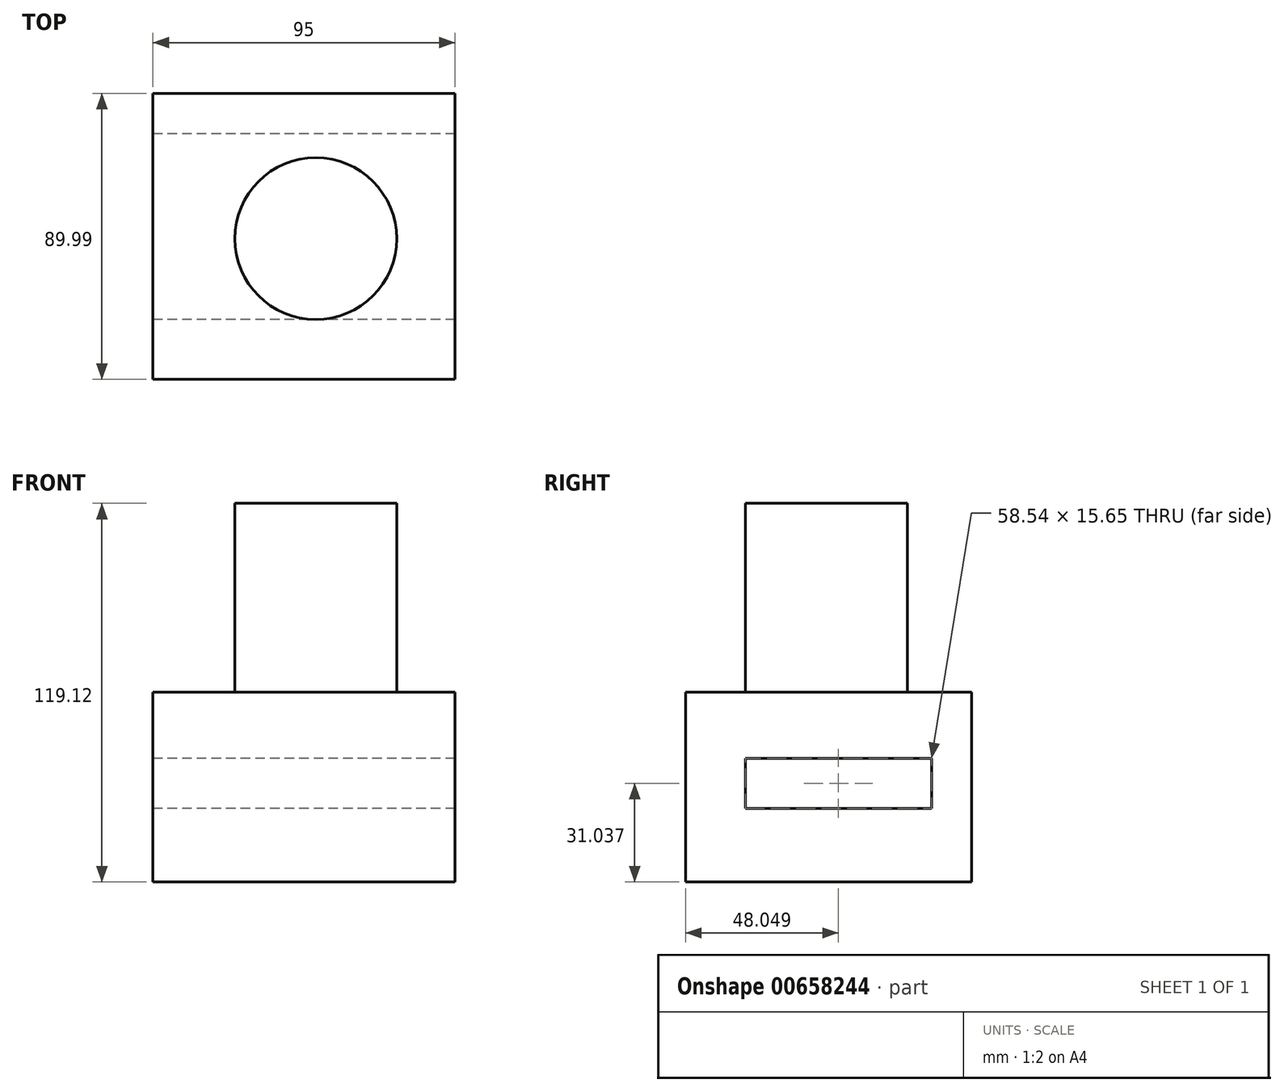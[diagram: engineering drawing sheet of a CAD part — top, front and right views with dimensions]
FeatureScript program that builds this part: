
annotation { "Feature Type Name" : "Feature", "Feature Type Description" : "" }
export const myFeature = defineFeature(function(context is Context, id is Id, definition is map)
    precondition{}
    {
        {
            var Q0;
            Q0=qCreatedBy(makeId("Right.planeOp"),FACE);
            var sketch = newSketch(context, id + "F0", { "sketchPlane" : qUnion([Q0])});
            skLineSegment(sketch, "E0.bottom", {"start": v(0, 0) * mm, "end": v(-90, 0) * mm});
            skLineSegment(sketch, "E0.top", {"start": v(0, 59.69) * mm, "end": v(-90, 59.69) * mm});
            skLineSegment(sketch, "E0.left", {"start": v(0, 0) * mm, "end": v(0, 59.69) * mm});
            skLineSegment(sketch, "E0.right", {"start": v(-90, 0) * mm, "end": v(-90, 59.69) * mm});
            skSolve(sketch);
        }
        {
            var Q0;
            Q0 = qSketchRegion(id + "F0", true);
            extrude(context, id + "F1", {"entities" : qUnion([Q0]), "depth" : 95 * mm, "offsetDistance" : 25.4 * mm});
        }
        {
            var Q0;
            Q0=makeQuery(id+"F1.opExtrude","SWEPT_FACE",FACE,{"disambiguationData":[OSD([sQuery(id+"F0.wireOp",EDGE,"E0.top")])]});
            var sketch = newSketch(context, id + "F2", { "sketchPlane" : qUnion([Q0])});
            skCircle(sketch, "E1", {"center": v(51.2, -45.7) * mm, "radius": 25.46 * mm});
            skSolve(sketch);
        }
        {
            var Q0;
            Q0 = qSketchRegion(id + "F2", true);
            extrude(context, id + "F3", {"entities" : qUnion([Q0]), "operationType" : NewBodyOperationType.ADD, "depth" : 59.44 * mm, "offsetDistance" : 25.4 * mm});
        }
        {
            var Q0;
            Q0=makeQuery(id+"F1.opExtrude","CAP_FACE",FACE,{"disambiguationData":[OSD([sQuery(id+"F0.wireOp",EDGE,"E0.bottom"),sQuery(id+"F0.wireOp",EDGE,"E0.top"),sQuery(id+"F0.wireOp",EDGE,"E0.left"),sQuery(id+"F0.wireOp",EDGE,"E0.right")])],"isStart":true});
            var sketch = newSketch(context, id + "F4", { "sketchPlane" : qUnion([Q0])});
            skLineSegment(sketch, "E2.bottom", {"start": v(12.67, 38.86) * mm, "end": v(71.21, 38.86) * mm});
            skLineSegment(sketch, "E2.top", {"start": v(12.67, 23.21) * mm, "end": v(71.21, 23.21) * mm});
            skLineSegment(sketch, "E2.left", {"start": v(12.67, 38.86) * mm, "end": v(12.67, 23.21) * mm});
            skLineSegment(sketch, "E2.right", {"start": v(71.21, 38.86) * mm, "end": v(71.21, 23.21) * mm});
            skSolve(sketch);
        }
        {
            var Q0;
            Q0=makeQuery(id+"F4.imprint","IMPRINT",FACE,{"disambiguationData":[TD([[makeQuery(id+"F4.imprint","IMPRINT",EDGE,{"derivedFrom":sQuery(id+"F4.wireOp",EDGE,"E2.bottom")}),-1.0]])]});
            extrude(context, id + "F5", {"entities" : qUnion([Q0]), "operationType" : NewBodyOperationType.REMOVE, "oppositeDirection" : true, "depth" : 116.08 * mm, "offsetDistance" : 25.4 * mm});
        }
    });
